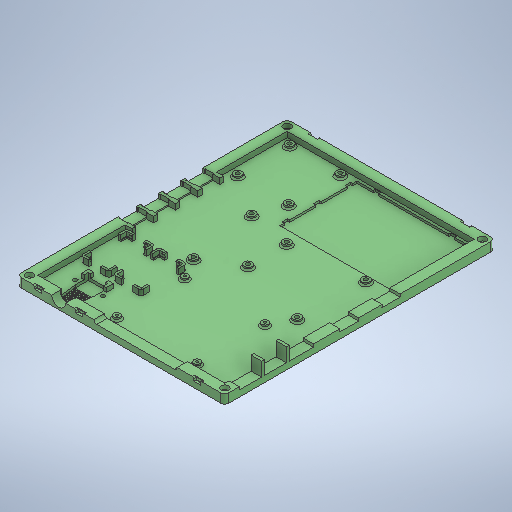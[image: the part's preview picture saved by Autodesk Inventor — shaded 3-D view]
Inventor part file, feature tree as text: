
AUTODESK INVENTOR PART (.ipt)
format: ipt  version: 2025.2 (Build 292293000, 293)  size: 1,185,280 bytes
history: native  units: mm
features: extrude x27, sketch x11, plane x10, fillet x6, mirror x5, pattern_linear x2, chamfer x1
ambient origin geometry x8: Origin, YZ Plane, XZ Plane, XY Plane, X Axis, Y Axis, Z Axis, Center Point
bodies: Solid1 (feature_tree)
feature tree (62):
  sketch  "Sketch1"  dims[d0=7.5mm d1=53.34mm]
  extrude  "Base"  Depth=7.5mm
  extrude  "Wall"  Depth=101.6mm
  extrude  "Breadboard slot"  Depth=2.54mm
  extrude  "Electronic mounting holes"  Depth=17.78mm
  chamfer  "Chamfer1"  Distance=0.5mm
  extrude  "Deeper mounting holes"  Depth=4.0mm
  extrude  "Extrusion14"  Depth=1.5mm
  extrude  "MT3608 base"  Depth=30.0mm
  extrude  "MT3608 wall"  Depth=2.0mm
  extrude  "MT3608 snap"  Depth=2.0mm
  plane  "Work Plane1"
  plane  "Work Plane2"
  fillet  "Fillet1"  Radius=2.0mm
  mirror  "Mirror1"
  mirror  "Mirror2"
  plane  "Work Plane3"
  mirror  "Mirror3"
  fillet  "Fillet2"  Radius=56.0mm
  extrude  "Extrusion9"  Depth=85.0mm
  extrude  "Extrusion10"  Depth=3.5mm
  extrude  "Extrusion11"  Depth=3.5mm
  sketch  "Sketch4"  dims[d6=50.8mm d7=17.78mm]
  extrude  "Board Ports"  Depth=2.0mm
  fillet  "Fillet6"  Radius=52.5mm
  extrude  "Extrusion22"  Depth=2.0mm
  extrude  "DC jack opening"  Depth=1.5mm
  fillet  "Fillet3"  Radius=2.0mm
  plane  "Work Plane4"
  plane  "Work Plane5"
  plane  "Work Plane6"
  plane  "Work Plane7"
  sketch  "Sketch6"  dims[d10=90.17mm]
  extrude  "Snap fit point 1"  Depth=43.0mm
  extrude  "Snap fit point 2"  Depth=17.3mm
  extrude  "Snap fit point 3"  Depth=30.3mm
  extrude  "Snap fit point 4"  Depth=2.0mm
  extrude  "Snap fit point 5"  Depth=2.0mm
  fillet  "Fillet4"  Radius=2.8mm
  fillet  "Fillet5"  Radius=1.5mm
  sketch  "Sketch12"  dims[d11=96.52mm]
  extrude  "Extrusion24"  Depth=1.5mm
  extrude  "Extrusion25"  Depth=2.0mm
  extrude  "Base mounting hole"  Depth=2.0mm
  plane  "Work Plane8"
  plane  "Work Plane9"
  mirror  "Mirror4"
  mirror  "Mirror5"
  extrude  "MT3608 snap fit test"  Depth=10.5mm
  plane  "Work Plane10"
  extrude  "DC Motor JST-PH Slot"  Depth=6.0mm
  sketch  "Sketch16"  dims[d15=54.75mm]
  extrude  "JST-PH reinforce"  Depth=14.0mm
  pattern_linear  "Rectangular Pattern2"  Count1=3  [1 undecoded]
  pattern_linear  "Rectangular Pattern1"  Spacing1=1.6mm  [1 undecoded]
  extrude  "JST-PH Connector Test"  Depth=2.0mm
  sketch  "Sketch Rectangular Pattern1"  dims[d2=101.6mm d3=15.24mm]
  sketch  "Sketch2"  dims[d4=13.97mm d5=2.54mm]
  sketch  "Sketch5"  dims[d9=66.04mm]
  sketch  "Sketch13"  dims[d12=45.72mm]
  sketch  "Sketch14"  dims[d13=2.8mm]
  sketch  "Sketch17"  dims[d16=81.68mm d17=0.5mm d18=4.0mm d19=1.5mm d20=30.0mm d22=22.7mm d23=10.0mm d25=10.0mm d27=11.9mm d28=54.53mm d29=2.0mm d31=56.0mm d32=85.0mm d33=3.5mm d34=3.5mm d35=1.8mm d37=52.5mm d38=61.5mm d39=1.5mm d40=2.0mm d44=43.0mm d46=17.3mm d47=30.0mm d48=17.0mm d49=30.3mm d50=2.871mm d51=3.32mm d52=2.8mm d54=1.5mm d55=1.5mm d56=40.244mm d57=40.057mm d59=10.5mm d62=6.0mm d63=14.0mm d64=30.0mm d65=1.6mm d66=0.8mm d67=1.2mm d68=0.8mm d69=1.2mm d70=0.8mm d71=1.2mm d72=0.8mm d73=1.2mm d74=0.8mm d75=1.2mm d76=0.8mm d77=9.5mm d78=13.0mm d79=10.5mm d80=4.5mm d81=3.0mm d82=2.0mm d83=2.0mm d84=1.5mm d86=0.5mm d87=2.5mm d88=0.0mm d89=4.0mm d90=0.0mm d91=1.5mm d92=0.0mm d93=2.0mm d94=0.0mm d95=1.0mm d96=0.0mm d97=1.0mm d98=0.0mm d99=4.0mm d100=0.0mm d101=4.0mm d102=1.5mm d103=4.0mm d104=4.0mm d105=4.0mm d106=4.0mm d107=4.0mm d108=1.5mm d109=45.0deg d110=2.0mm d111=0.0mm d112=0.3mm d113=2.0mm d116=3.0mm d117=2.0mm d118=0.0mm d119=0.5mm d120=0.0mm d121=3.0mm d122=0.0mm d123=4.0mm d124=4.0mm d125=1.0mm d127=19.0mm d129=37.0mm d131=8.5mm d132=13.64mm d133=39.0mm d134=13.0mm d135=2.0mm d136=0.0mm d137=25.0mm d138=85.0mm d139=10.0mm d140=2.0mm d141=0.0mm d142=3.0mm d143=20.0mm d144=6.5mm d145=2.5mm d146=0.0mm d147=3.0mm d148=1.5mm d149=2.5mm d150=1.0mm d151=45.0deg d154=-20.0mm d155=-105.0mm d157=-130.0mm d158=5.0mm d159=0.0mm d160=5.0mm d161=0.0mm d162=-135.0mm d163=5.0mm d164=0.0mm d165=5.0mm d166=0.0mm d167=5.0mm d168=0.0mm d173=65.0mm d174=180.0mm d175=135.0mm d176=17.0mm d177=35.0mm d178=54.5mm d179=1.0mm d180=8.0mm d181=0.0mm d188=1.0mm d189=5.8mm d190=4.5mm d191=4.5mm d192=5.5mm d193=1.0mm d194=0.0mm d195=3.2mm d196=0.0mm d197=0.0mm d198=3.0mm d199=0.0mm d200=0.0mm d201=0.0mm d202=4.0mm d203=6.2mm d204=14.0mm d205=12.9mm d213=115.0mm d214=3.0mm d215=0.0mm d216=40.0mm d218=16.0mm d224=1.3mm d225=9.0mm d226=5.0mm d227=10.0mm d228=0.0mm d231=40.0mm d233=16.0mm d234=2.0mm d235=10.0mm d236=0.0mm d237=1.0mm d238=2.0mm d239=45.0deg]
note: 2 required parameter values undecoded (feature->parameter linkage not recoverable at this tier; creation-order binding heuristic only, values carry confidence <= 0.55)
